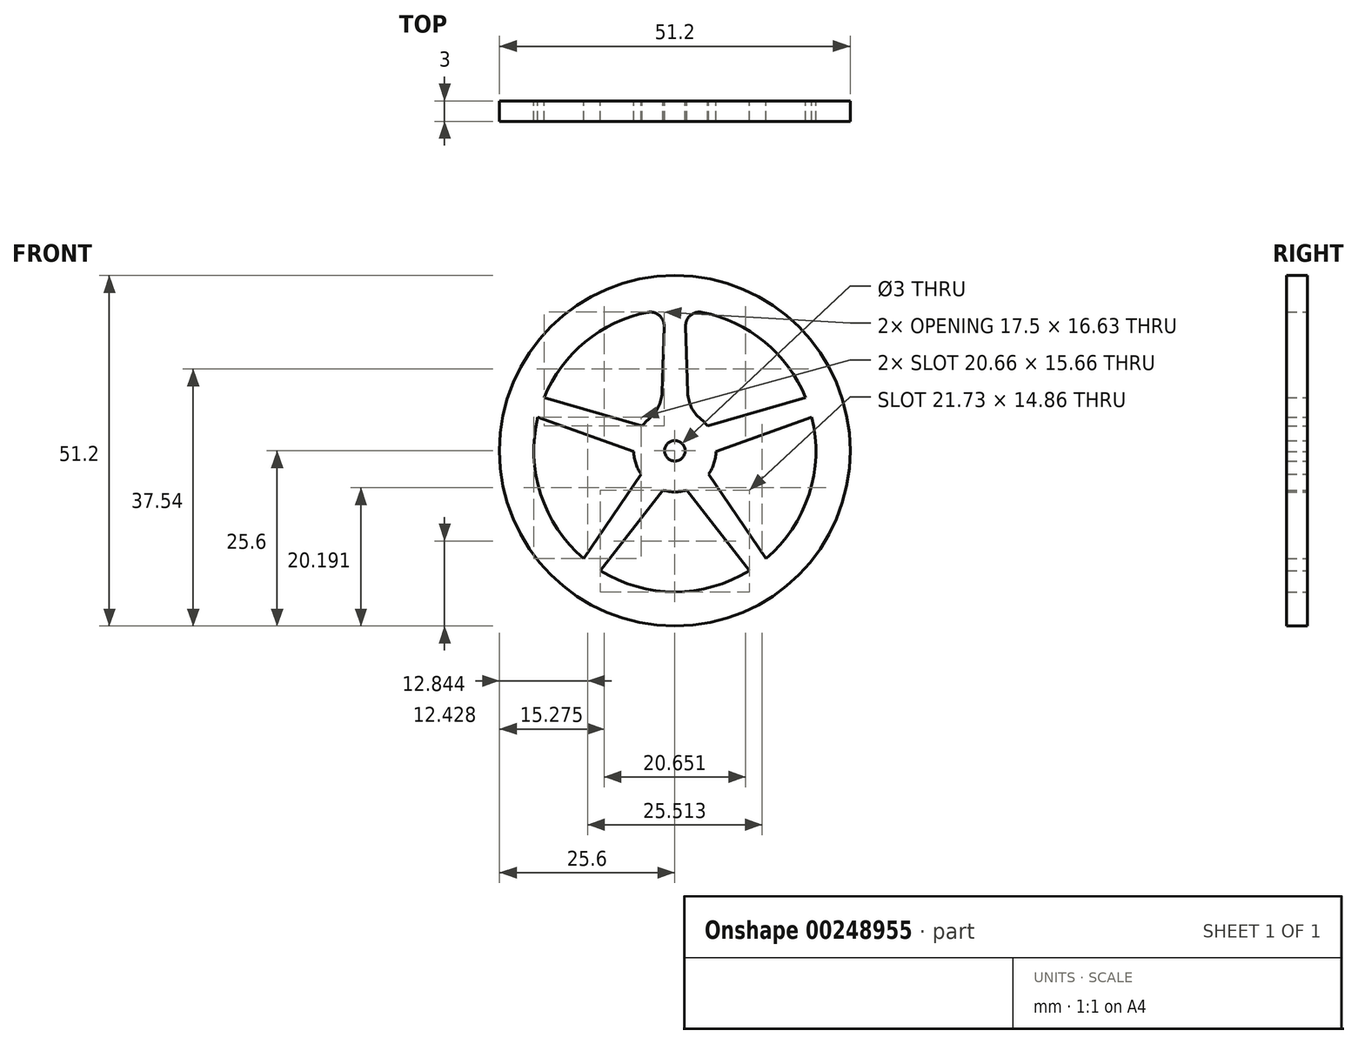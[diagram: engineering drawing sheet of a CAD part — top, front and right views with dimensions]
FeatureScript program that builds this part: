
annotation { "Feature Type Name" : "Feature", "Feature Type Description" : "" }
export const myFeature = defineFeature(function(context is Context, id is Id, definition is map)
    precondition{}
    {
        {
            var Q0;
            Q0=qCreatedBy(makeId("Front.planeOp"),FACE);
            var sketch = newSketch(context, id + "F0", { "sketchPlane" : qUnion([Q0])});
            skCircle(sketch, "E0", {"center": v(0, 0) * mm, "radius": 25.6 * mm});
            skCircle(sketch, "E1", {"center": v(0, 0) * mm, "radius": 1.5 * mm});
            skCircle(sketch, "E2", {"center": v(0, 0) * mm, "radius": 6 * mm});
            skCircle(sketch, "E3", {"center": v(0, 0) * mm, "radius": 20.6 * mm});
            skLineSegment(sketch, "E4.trimOffspring", {"start": v(0, 6) * mm, "end": v(0, 20.6) * mm, "construction": true});
            skLineSegment(sketch, "E5.trimOffspring", {"start": v(0, 25.6) * mm, "end": v(0, 28.2) * mm, "construction": true});
            skLineSegment(sketch, "E6", {"start": v(-1.97, 5.67) * mm, "end": v(-1.5, 20.55) * mm});
            skLineSegment(sketch, "E7.MirrorCS", {"start": v(1.5, 20.55) * mm, "end": v(1.5, 20.55) * mm});
            skPoint(sketch, "E8.orphan", {"position": v(1.97, 5.67) * mm});
            skLineSegment(sketch, "E9.MirrorCS", {"start": v(1.97, 5.67) * mm, "end": v(1.5, 20.55) * mm});
            skSolve(sketch);
        }
        {
            var Q0;
            Q0=makeQuery(id+"F0.imprint","IMPRINT",FACE,{"disambiguationData":[TD([[makeQuery(id+"F0.imprint","IMPRINT",EDGE,{"derivedFrom":sQuery(id+"F0.wireOp",EDGE,"E0")}),1.0]])]});
            var Q1;
            Q1=makeQuery(id+"F0.imprint","IMPRINT",FACE,{"disambiguationData":[TD([[makeQuery(id+"F0.imprint","IMPRINT",EDGE,{"derivedFrom":sQuery(id+"F0.wireOp",EDGE,"E1")}),-1.0]])]});
            var Q2;
            {var subQ0=sQuery(id+"F0.wireOp",EDGE,"E6");Q2=makeQuery(id+"F0.imprint","IMPRINT",FACE,{"disambiguationData":[TD([[makeQuery(id+"F0.imprint","IMPRINT",EDGE,{"derivedFrom":subQ0}),-1.0]])]});}
            var Q3;
            Q3=sQuery(id+"F0.wireOp",EDGE,"E1");
            var Q4;
            Q4=sQuery(id+"F0.wireOp",EDGE,"E0");
            extrude(context, id + "F1", {"entities" : qUnion([Q0, Q1, Q2]), "surfaceEntities" : qUnion([Q3, Q4]), "depth" : 3 * mm});
        }
        {
            var Q0;
            Q0=makeQuery(id+"F1.opExtrude","SWEPT_BODY",BODY,{"disambiguationData":[OSD([sQuery(id+"F0.wireOp",EDGE,"E0"),sQuery(id+"F0.wireOp",EDGE,"E1"),sQuery(id+"F0.wireOp",EDGE,"E2"),sQuery(id+"F0.wireOp",EDGE,"E3"),sQuery(id+"F0.wireOp",EDGE,"E6"),sQuery(id+"F0.wireOp",EDGE,"E9.MirrorCS")])]});
            var Q1;
            Q1=sQuery(id+"F0.wireOp",EDGE,"E3");
            circularPattern(context, id + "F2", {"operationType" : NewBodyOperationType.ADD, "entities" : qUnion([Q0]), "axis" : qUnion([Q1]), "angle" : 360 * degree, "instanceCount" : 5, "equalSpace" : true});
        }
        {
            var Q0;
            Q0=makeQuery(id+"F1.opExtrude","SWEPT_EDGE",EDGE,{"disambiguationData":[OSD([sQuery(id+"F0.wireOp",EDGE,"E2"),sQuery(id+"F0.wireOp",EDGE,"E9.MirrorCS")])]});
            var Q1;
            Q1=makeQuery(id+"F2.opPattern","COPY",EDGE,{"derivedFrom":makeQuery(id+"F1.opExtrude","SWEPT_EDGE",EDGE,{"disambiguationData":[OSD([sQuery(id+"F0.wireOp",EDGE,"E2"),sQuery(id+"F0.wireOp",EDGE,"E6")])]}),"instanceName":"4"});
            var Q2;
            Q2=makeQuery(id+"F2.opPattern","COPY",EDGE,{"derivedFrom":makeQuery(id+"F1.opExtrude","SWEPT_EDGE",EDGE,{"disambiguationData":[OSD([sQuery(id+"F0.wireOp",EDGE,"E2"),sQuery(id+"F0.wireOp",EDGE,"E6")])]}),"instanceName":"3"});
            var Q3;
            Q3=makeQuery(id+"F1.opExtrude","SWEPT_EDGE",EDGE,{"disambiguationData":[OSD([sQuery(id+"F0.wireOp",EDGE,"E2"),sQuery(id+"F0.wireOp",EDGE,"E6")])]});
            var Q4;
            Q4=makeQuery(id+"F2.opPattern","COPY",EDGE,{"derivedFrom":makeQuery(id+"F1.opExtrude","SWEPT_EDGE",EDGE,{"disambiguationData":[OSD([sQuery(id+"F0.wireOp",EDGE,"E2"),sQuery(id+"F0.wireOp",EDGE,"E9.MirrorCS")])]}),"instanceName":"1"});
            var Q5;
            Q5=makeQuery(id+"F2.opPattern","COPY",EDGE,{"derivedFrom":makeQuery(id+"F1.opExtrude","SWEPT_EDGE",EDGE,{"disambiguationData":[OSD([sQuery(id+"F0.wireOp",EDGE,"E2"),sQuery(id+"F0.wireOp",EDGE,"E6")])]}),"instanceName":"1"});
            var Q6;
            Q6=makeQuery(id+"F2.opPattern","COPY",EDGE,{"derivedFrom":makeQuery(id+"F1.opExtrude","SWEPT_EDGE",EDGE,{"disambiguationData":[OSD([sQuery(id+"F0.wireOp",EDGE,"E2"),sQuery(id+"F0.wireOp",EDGE,"E9.MirrorCS")])]}),"instanceName":"2"});
            var Q7;
            Q7=makeQuery(id+"F2.opPattern","COPY",EDGE,{"derivedFrom":makeQuery(id+"F1.opExtrude","SWEPT_EDGE",EDGE,{"disambiguationData":[OSD([sQuery(id+"F0.wireOp",EDGE,"E2"),sQuery(id+"F0.wireOp",EDGE,"E6")])]}),"instanceName":"2"});
            var Q8;
            Q8=makeQuery(id+"F2.opPattern","COPY",EDGE,{"derivedFrom":makeQuery(id+"F1.opExtrude","SWEPT_EDGE",EDGE,{"disambiguationData":[OSD([sQuery(id+"F0.wireOp",EDGE,"E2"),sQuery(id+"F0.wireOp",EDGE,"E9.MirrorCS")])]}),"instanceName":"3"});
            var Q9;
            Q9=makeQuery(id+"F2.opPattern","COPY",EDGE,{"derivedFrom":makeQuery(id+"F1.opExtrude","SWEPT_EDGE",EDGE,{"disambiguationData":[OSD([sQuery(id+"F0.wireOp",EDGE,"E2"),sQuery(id+"F0.wireOp",EDGE,"E9.MirrorCS")])]}),"instanceName":"4"});
            var Q10;
            {var subQ0=makeQuery(id+"F1.opExtrude","SWEPT_FACE",FACE,{"disambiguationData":[OSD([sQuery(id+"F0.wireOp",EDGE,"E2")])]});Q10=makeQuery(id+"F2.boolean.opBoolean","INTERSECT",EDGE,{"disambiguationData":[OD(1.0)],"derivedFrom":[makeQuery(id+"F2.opPattern","COPY",FACE,{"derivedFrom":subQ0,"instanceName":"1"}),makeQuery(id+"F2.opPattern","COPY",FACE,{"derivedFrom":subQ0,"instanceName":"2"}),makeQuery(id+"F2.opPattern","COPY",FACE,{"derivedFrom":subQ0,"instanceName":"3"})]});}
            var Q11;
            {var subQ0=makeQuery(id+"F1.opExtrude","SWEPT_FACE",FACE,{"disambiguationData":[OSD([sQuery(id+"F0.wireOp",EDGE,"E2")])]});Q11=makeQuery(id+"F2.boolean.opBoolean","INTERSECT",EDGE,{"disambiguationData":[OD(1.0)],"derivedFrom":[makeQuery(id+"F2.opPattern","COPY",FACE,{"derivedFrom":subQ0,"instanceName":"1"}),makeQuery(id+"F2.opPattern","COPY",FACE,{"derivedFrom":subQ0,"instanceName":"2"}),makeQuery(id+"F2.opPattern","COPY",FACE,{"derivedFrom":subQ0,"instanceName":"4"})]});}
            var Q12;
            {var subQ0=makeQuery(id+"F1.opExtrude","SWEPT_FACE",FACE,{"disambiguationData":[OSD([sQuery(id+"F0.wireOp",EDGE,"E2")])]});Q12=makeQuery(id+"F2.boolean.opBoolean","INTERSECT",EDGE,{"disambiguationData":[OD(0.0)],"derivedFrom":[makeQuery(id+"F2.opPattern","COPY",FACE,{"derivedFrom":subQ0,"instanceName":"1"}),makeQuery(id+"F2.opPattern","COPY",FACE,{"derivedFrom":subQ0,"instanceName":"3"})]});}
            var Q13;
            {var subQ0=makeQuery(id+"F1.opExtrude","SWEPT_FACE",FACE,{"disambiguationData":[OSD([sQuery(id+"F0.wireOp",EDGE,"E2")])]});Q13=makeQuery(id+"F2.boolean.opBoolean","INTERSECT",EDGE,{"disambiguationData":[OD(1.0)],"derivedFrom":[makeQuery(id+"F2.opPattern","COPY",FACE,{"derivedFrom":subQ0,"instanceName":"1"}),makeQuery(id+"F2.opPattern","COPY",FACE,{"derivedFrom":subQ0,"instanceName":"3"})]});}
            var Q14;
            {var subQ0=makeQuery(id+"F1.opExtrude","SWEPT_FACE",FACE,{"disambiguationData":[OSD([sQuery(id+"F0.wireOp",EDGE,"E2")])]});Q14=makeQuery(id+"F2.boolean.opBoolean","INTERSECT",EDGE,{"disambiguationData":[OD(0.0)],"derivedFrom":[makeQuery(id+"F2.opPattern","COPY",FACE,{"derivedFrom":subQ0,"instanceName":"1"}),makeQuery(id+"F2.opPattern","COPY",FACE,{"derivedFrom":subQ0,"instanceName":"2"}),makeQuery(id+"F2.opPattern","COPY",FACE,{"derivedFrom":subQ0,"instanceName":"3"})]});}
            var Q15;
            {var subQ0=makeQuery(id+"F1.opExtrude","SWEPT_FACE",FACE,{"disambiguationData":[OSD([sQuery(id+"F0.wireOp",EDGE,"E2")])]});Q15=makeQuery(id+"F2.boolean.opBoolean","INTERSECT",EDGE,{"disambiguationData":[OD(0.0)],"derivedFrom":[makeQuery(id+"F2.opPattern","COPY",FACE,{"derivedFrom":subQ0,"instanceName":"1"}),makeQuery(id+"F2.opPattern","COPY",FACE,{"derivedFrom":subQ0,"instanceName":"2"}),makeQuery(id+"F2.opPattern","COPY",FACE,{"derivedFrom":subQ0,"instanceName":"4"})]});}
            fillet(context, id + "F3", {"entities" : qUnion([Q0, Q1, Q2, Q3, Q4, Q5, Q6, Q7, Q8, Q9, Q10, Q11, Q12, Q13, Q14, Q15]), "radius" : 5.08 * mm, "tangentPropagation" : true, "allowEdgeOverflow" : false});
        }
        {
            var Q0;
            Q0=makeQuery(id+"F1.opExtrude","SWEPT_EDGE",EDGE,{"disambiguationData":[OSD([sQuery(id+"F0.wireOp",EDGE,"E3"),sQuery(id+"F0.wireOp",EDGE,"E9.MirrorCS")])]});
            var Q1;
            Q1=makeQuery(id+"F2.opPattern","COPY",EDGE,{"derivedFrom":makeQuery(id+"F1.opExtrude","SWEPT_EDGE",EDGE,{"disambiguationData":[OSD([sQuery(id+"F0.wireOp",EDGE,"E3"),sQuery(id+"F0.wireOp",EDGE,"E6")])]}),"instanceName":"1"});
            var Q2;
            Q2=makeQuery(id+"F2.opPattern","COPY",EDGE,{"derivedFrom":makeQuery(id+"F1.opExtrude","SWEPT_EDGE",EDGE,{"disambiguationData":[OSD([sQuery(id+"F0.wireOp",EDGE,"E3"),sQuery(id+"F0.wireOp",EDGE,"E9.MirrorCS")])]}),"instanceName":"4"});
            var Q3;
            Q3=makeQuery(id+"F2.opPattern","COPY",EDGE,{"derivedFrom":makeQuery(id+"F1.opExtrude","SWEPT_EDGE",EDGE,{"disambiguationData":[OSD([sQuery(id+"F0.wireOp",EDGE,"E3"),sQuery(id+"F0.wireOp",EDGE,"E9.MirrorCS")])]}),"instanceName":"3"});
            var Q4;
            Q4=makeQuery(id+"F1.opExtrude","SWEPT_EDGE",EDGE,{"disambiguationData":[OSD([sQuery(id+"F0.wireOp",EDGE,"E3"),sQuery(id+"F0.wireOp",EDGE,"E6")])]});
            var Q5;
            Q5=makeQuery(id+"F2.opPattern","COPY",EDGE,{"derivedFrom":makeQuery(id+"F1.opExtrude","SWEPT_EDGE",EDGE,{"disambiguationData":[OSD([sQuery(id+"F0.wireOp",EDGE,"E3"),sQuery(id+"F0.wireOp",EDGE,"E6")])]}),"instanceName":"4"});
            var Q6;
            Q6=makeQuery(id+"F2.opPattern","COPY",EDGE,{"derivedFrom":makeQuery(id+"F1.opExtrude","SWEPT_EDGE",EDGE,{"disambiguationData":[OSD([sQuery(id+"F0.wireOp",EDGE,"E3"),sQuery(id+"F0.wireOp",EDGE,"E6")])]}),"instanceName":"3"});
            var Q7;
            Q7=makeQuery(id+"F2.opPattern","COPY",EDGE,{"derivedFrom":makeQuery(id+"F1.opExtrude","SWEPT_EDGE",EDGE,{"disambiguationData":[OSD([sQuery(id+"F0.wireOp",EDGE,"E3"),sQuery(id+"F0.wireOp",EDGE,"E9.MirrorCS")])]}),"instanceName":"1"});
            var Q8;
            Q8=makeQuery(id+"F2.opPattern","COPY",EDGE,{"derivedFrom":makeQuery(id+"F1.opExtrude","SWEPT_EDGE",EDGE,{"disambiguationData":[OSD([sQuery(id+"F0.wireOp",EDGE,"E3"),sQuery(id+"F0.wireOp",EDGE,"E6")])]}),"instanceName":"2"});
            var Q9;
            Q9=makeQuery(id+"F2.opPattern","COPY",EDGE,{"derivedFrom":makeQuery(id+"F1.opExtrude","SWEPT_EDGE",EDGE,{"disambiguationData":[OSD([sQuery(id+"F0.wireOp",EDGE,"E3"),sQuery(id+"F0.wireOp",EDGE,"E9.MirrorCS")])]}),"instanceName":"2"});
            var Q10;
            {var subQ0=makeQuery(id+"F1.opExtrude","SWEPT_FACE",FACE,{"disambiguationData":[OSD([sQuery(id+"F0.wireOp",EDGE,"E3")])]});Q10=makeQuery(id+"F2.boolean.opBoolean","INTERSECT",EDGE,{"disambiguationData":[OD(1.0)],"derivedFrom":[makeQuery(id+"F2.opPattern","COPY",FACE,{"derivedFrom":subQ0,"instanceName":"1"}),makeQuery(id+"F2.opPattern","COPY",FACE,{"derivedFrom":subQ0,"instanceName":"2"}),makeQuery(id+"F2.opPattern","COPY",FACE,{"derivedFrom":subQ0,"instanceName":"3"})]});}
            var Q11;
            {var subQ0=makeQuery(id+"F1.opExtrude","SWEPT_FACE",FACE,{"disambiguationData":[OSD([sQuery(id+"F0.wireOp",EDGE,"E3")])]});Q11=makeQuery(id+"F2.boolean.opBoolean","INTERSECT",EDGE,{"disambiguationData":[OD(1.0)],"derivedFrom":[makeQuery(id+"F2.opPattern","COPY",FACE,{"derivedFrom":subQ0,"instanceName":"1"}),makeQuery(id+"F2.opPattern","COPY",FACE,{"derivedFrom":subQ0,"instanceName":"2"}),makeQuery(id+"F2.opPattern","COPY",FACE,{"derivedFrom":subQ0,"instanceName":"4"})]});}
            var Q12;
            {var subQ0=makeQuery(id+"F1.opExtrude","SWEPT_FACE",FACE,{"disambiguationData":[OSD([sQuery(id+"F0.wireOp",EDGE,"E3")])]});Q12=makeQuery(id+"F2.boolean.opBoolean","INTERSECT",EDGE,{"disambiguationData":[OD(0.0)],"derivedFrom":[makeQuery(id+"F2.opPattern","COPY",FACE,{"derivedFrom":subQ0,"instanceName":"1"}),makeQuery(id+"F2.opPattern","COPY",FACE,{"derivedFrom":subQ0,"instanceName":"3"})]});}
            var Q13;
            {var subQ0=makeQuery(id+"F1.opExtrude","SWEPT_FACE",FACE,{"disambiguationData":[OSD([sQuery(id+"F0.wireOp",EDGE,"E3")])]});Q13=makeQuery(id+"F2.boolean.opBoolean","INTERSECT",EDGE,{"disambiguationData":[OD(1.0)],"derivedFrom":[makeQuery(id+"F2.opPattern","COPY",FACE,{"derivedFrom":subQ0,"instanceName":"1"}),makeQuery(id+"F2.opPattern","COPY",FACE,{"derivedFrom":subQ0,"instanceName":"3"})]});}
            var Q14;
            {var subQ0=makeQuery(id+"F1.opExtrude","SWEPT_FACE",FACE,{"disambiguationData":[OSD([sQuery(id+"F0.wireOp",EDGE,"E3")])]});Q14=makeQuery(id+"F2.boolean.opBoolean","INTERSECT",EDGE,{"disambiguationData":[OD(0.0)],"derivedFrom":[makeQuery(id+"F2.opPattern","COPY",FACE,{"derivedFrom":subQ0,"instanceName":"1"}),makeQuery(id+"F2.opPattern","COPY",FACE,{"derivedFrom":subQ0,"instanceName":"2"}),makeQuery(id+"F2.opPattern","COPY",FACE,{"derivedFrom":subQ0,"instanceName":"4"})]});}
            var Q15;
            {var subQ0=makeQuery(id+"F1.opExtrude","SWEPT_FACE",FACE,{"disambiguationData":[OSD([sQuery(id+"F0.wireOp",EDGE,"E3")])]});Q15=makeQuery(id+"F2.boolean.opBoolean","INTERSECT",EDGE,{"disambiguationData":[OD(0.0)],"derivedFrom":[makeQuery(id+"F2.opPattern","COPY",FACE,{"derivedFrom":subQ0,"instanceName":"1"}),makeQuery(id+"F2.opPattern","COPY",FACE,{"derivedFrom":subQ0,"instanceName":"2"}),makeQuery(id+"F2.opPattern","COPY",FACE,{"derivedFrom":subQ0,"instanceName":"3"})]});}
            fillet(context, id + "F4", {"entities" : qUnion([Q0, Q1, Q2, Q3, Q4, Q5, Q6, Q7, Q8, Q9, Q10, Q11, Q12, Q13, Q14, Q15]), "radius" : 2 * mm, "tangentPropagation" : true, "allowEdgeOverflow" : false});
        }
    });
